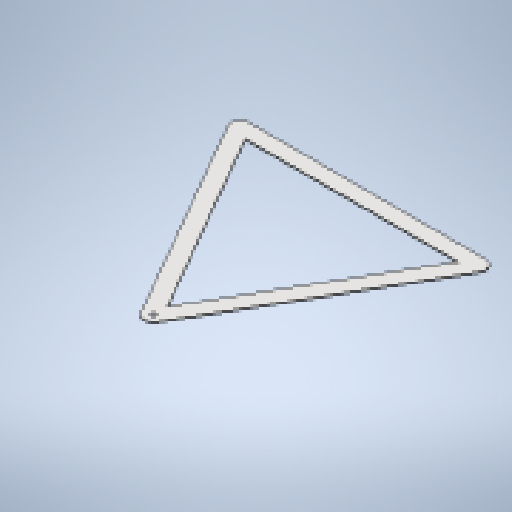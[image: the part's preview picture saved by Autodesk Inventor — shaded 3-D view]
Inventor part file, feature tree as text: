
AUTODESK INVENTOR PART (.ipt)
format: ipt  version: 2025.1 (Build 291241020, 241B)  size: 196,608 bytes
history: native  units: mm
features: other x2, sheet_metal_op x1, chamfer x1, sketch x1
ambient origin geometry x8: Origin, YZ Plane, XZ Plane, XY Plane, X Axis, Y Axis, Z Axis, Center Point
bodies: Solid1 (feature_tree)
feature tree (5):
  sheet_metal_op  "Face1"
  chamfer  "Corner Round3"
  sketch  "Sketch1"  dims[d2=3.0mm d34=17.0mm d35=20.0mm d36=1000.25mm d37=1000.25mm d38=50.0mm d39=17.0mm d40=17.0mm d41=6.0mm]
  other  "Plate1"
  other  "Definition1"
